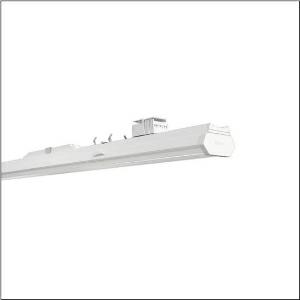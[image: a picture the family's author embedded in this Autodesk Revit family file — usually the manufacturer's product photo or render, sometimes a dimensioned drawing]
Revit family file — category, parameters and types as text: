
# Revit family: licross_r__11_protected_ho_51td13cn4e5s_07e4
name_source: partatom
category: Lighting Fixtures
units: mm (PartAtom-declared; Revit-internal decimal feet)

## family parameters
Cut with Voids When Loaded = No
Host = Face
Light Source = No
Part Type = Normal
Room Calculation Point = No
Round Connector Dimension = Use Diameter
Shared = No

## types (1)
- --- (1 x LED, 14500 lm, 77.6 W, 4000K)
    Apparent Load = 78 VA
    CIE Flux Codes = 89 96 99 100 99
    Color Rendering = 80
    Color Temperature = 4000K
    Default Elevation = 1800 mm
    Description = Licross® 11 Protected HO, luminaire insert, of sheet steel, galvanised, coil coated, white, length: 1.500mm, width: 90mm, height: 101mm, LED rated luminous flux: 14.500lm, light colour: 840, control gear: ON/OFF Multilumen, CLOi, with plug, 3-pole, with phase selection, mains connection: 220..240V, AC, 50/60Hz, start of lifetime: 78W, end of service life: 87W, internal wiring halogen-free, primary light control with lens, of plastic, primary optical cover: cover, of PMMA, light emission: direct distribution, primary light characteristic: symmetric, protection rating (complete): IP54, insulation class (complete): insulation class I (protective earthing), certification: CE, ENEC, VDE, UKCA, protection symbol: D if used in an environment with non-conductive dust loads with corresponding accessories, impact resistance: IK06, permissible ambient temperature for indoor applications: -35..+35°C, corresponds to IFS (International Featured Standards) requirements for safety and quality in the food industry, reducing of maximum allowable ambient temperature of 5°C with ceiling mounting, LABS conformity tested according to VDMA 24364:2018-05, packaging unit: 1 piece
    Height = 92 mm
    Lamp = 1 x LED
    Lamp Light Flux = 14500 lm
    Lamp Power = 77.6 W
    Lamp count = 1
    Length = 1500 mm
    Luminous efficacy = 187 lm/W
    Manufacturer = Siteco
    ModVariant = No
    Model = 51TD13CN4E5S
    Mounting Place = Ceiling
    Mounting Type = Pendant
    Number of Poles = 1
    OnlyDefault = Yes
    Power Factor = 1
    Product Name = Licross® 11 Protected HO
    Product group = luminaire insert | ceiling pendant
    ProductGroupID = 902
    Protection Class = Protection class I
    Protection Degree = IP 54
    RLX_Detail_Level = 1
    RLX_Emergency_Light_Flux = 0 lm
    RLX_Emergency_Type = 0
    RLX_Emergency_Type_DB = No
    RlxData = <blob elided: 22089 chars, md5=5cf50192>
    Socket = socket
    Standby Power = 0 W
    System Light Flux = 14500 lm
    System Power = 78 W
    Type Comments = factory setting: luminous flux: 100 % | (A | C | E) | 181 mA
    Type Image = l_1256145.jpg
    URL = http://relux.com
    VarID = @adj_107209
    Voltage = 0 V
    Weight = 0.00 kg
    Width = 88 mm

## geometry (parser evidence)
native form markers: Blend x4, Sweep x11
no freeform markers — native parametric forms only
